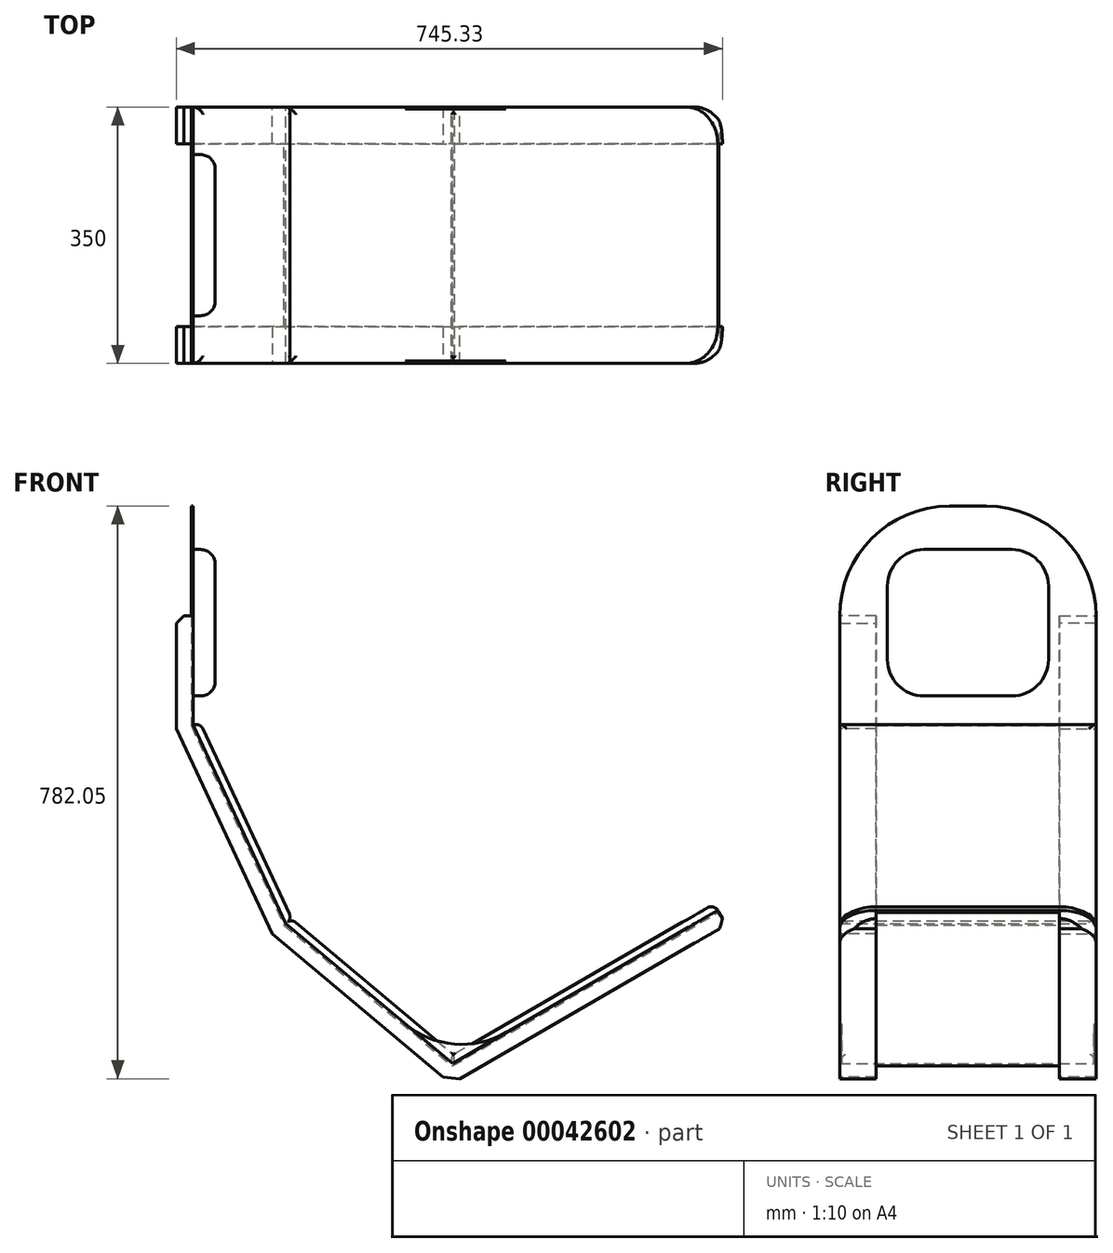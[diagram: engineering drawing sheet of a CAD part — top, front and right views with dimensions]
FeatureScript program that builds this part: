
annotation { "Feature Type Name" : "Feature", "Feature Type Description" : "" }
export const myFeature = defineFeature(function(context is Context, id is Id, definition is map)
    precondition{}
    {
        {
            var Q0;
            Q0=qCreatedBy(makeId("Front.planeOp"),FACE);
            var sketch = newSketch(context, id + "F0", { "sketchPlane" : qUnion([Q0])});
            skLineSegment(sketch, "E0", {"start": v(0, 770) * mm, "end": v(0, 0) * mm, "construction": true});
            skLineSegment(sketch, "E1", {"start": v(0, 770) * mm, "end": v(0, 470) * mm});
            skLineSegment(sketch, "E2", {"start": v(0, 470) * mm, "end": v(126.79, 198.1) * mm});
            skLineSegment(sketch, "E3", {"start": v(126.79, 198.1) * mm, "end": v(356.6, 5.27) * mm});
            skLineSegment(sketch, "E4", {"start": v(356.6, 5.27) * mm, "end": v(720.33, 215.27) * mm});
            skLineSegment(sketch, "E5", {"start": v(0, 0) * mm, "end": v(1241.59, 0) * mm, "construction": true});
            skLineSegment(sketch, "E6.0", {"start": v(356.92, 8.92) * mm, "end": v(718.83, 217.87) * mm});
            skLineSegment(sketch, "E6.1", {"start": v(129.22, 199.98) * mm, "end": v(356.92, 8.92) * mm});
            skLineSegment(sketch, "E6.2", {"start": v(3, 470.67) * mm, "end": v(129.22, 199.98) * mm});
            skLineSegment(sketch, "E6.3", {"start": v(3, 770) * mm, "end": v(3, 470.67) * mm});
            skLineSegment(sketch, "E7", {"start": v(718.83, 217.87) * mm, "end": v(720.33, 215.27) * mm});
            skLineSegment(sketch, "E8", {"start": v(0, 770) * mm, "end": v(3, 770) * mm});
            skSolve(sketch);
        }
        {
            var Q0;
            Q0=qSketchRegion(id+"F0",true);
            extrude(context, id + "F1", {"entities" : qUnion([Q0]), "endBound" : BoundingType.SYMMETRIC, "depth" : 350 * mm});
        }
        {
            var Q0;
            Q0=makeQuery(id+"F1.opExtrude","CAP_EDGE",EDGE,{"disambiguationData":[OSD([sQuery(id+"F0.wireOp",EDGE,"E8")])],"isStart":false});
            var Q1;
            Q1=makeQuery(id+"F1.opExtrude","CAP_EDGE",EDGE,{"disambiguationData":[OSD([sQuery(id+"F0.wireOp",EDGE,"E8")])],"isStart":true});
            fillet(context, id + "F2", {"entities" : qUnion([Q0, Q1]), "radius" : 150 * mm, "tangentPropagation" : true, "allowEdgeOverflow" : false});
        }
        {
            var Q0;
            Q0=makeQuery(id+"F1.opExtrude","CAP_FACE",FACE,{"disambiguationData":[OSD([sQuery(id+"F0.wireOp",EDGE,"E1"),sQuery(id+"F0.wireOp",EDGE,"E2"),sQuery(id+"F0.wireOp",EDGE,"E3"),sQuery(id+"F0.wireOp",EDGE,"E4"),sQuery(id+"F0.wireOp",EDGE,"E6.0"),sQuery(id+"F0.wireOp",EDGE,"E6.1"),sQuery(id+"F0.wireOp",EDGE,"E6.2"),sQuery(id+"F0.wireOp",EDGE,"E6.3"),sQuery(id+"F0.wireOp",EDGE,"E7"),sQuery(id+"F0.wireOp",EDGE,"E8")])],"isStart":false});
            var sketch = newSketch(context, id + "F3", { "sketchPlane" : qUnion([Q0])});
            skLineSegment(sketch, "E9.0", {"start": v(129.22, 199.98) * mm, "end": v(356.92, 8.92) * mm});
            skLineSegment(sketch, "E9.1", {"start": v(356.92, 8.92) * mm, "end": v(718.83, 217.87) * mm});
            skArc(sketch, "E10", {"start": v(292.55, 62.93) * mm, "mid": v(359.23, 35.31) * mm, "end": v(429.69, 50.93) * mm});
            skSolve(sketch);
        }
        {
            var Q0;
            Q0=qSketchRegion(id+"F3",true);
            extrude(context, id + "F4", {"entities" : qUnion([Q0]), "oppositeDirection" : true, "depth" : 3 * mm});
        }
        {
            var Q0;
            Q0=makeQuery(id+"F4.opExtrude","SWEPT_BODY",BODY,{"disambiguationData":[OSD([sQuery(id+"F3.wireOp",EDGE,"E9.0"),sQuery(id+"F3.wireOp",EDGE,"E9.1"),sQuery(id+"F3.wireOp",EDGE,"E10")])]});
            var Q1;
            Q1=qCreatedBy(makeId("Front.planeOp"),FACE);
            mirror(context, id + "F5", {"entities" : qUnion([Q0]), "mirrorPlane" : qUnion([Q1])});
        }
        {
            var Q0;
            Q0=makeQuery(id+"F1.opExtrude","CAP_FACE",FACE,{"disambiguationData":[OSD([sQuery(id+"F0.wireOp",EDGE,"E1"),sQuery(id+"F0.wireOp",EDGE,"E2"),sQuery(id+"F0.wireOp",EDGE,"E3"),sQuery(id+"F0.wireOp",EDGE,"E4"),sQuery(id+"F0.wireOp",EDGE,"E6.0"),sQuery(id+"F0.wireOp",EDGE,"E6.1"),sQuery(id+"F0.wireOp",EDGE,"E6.2"),sQuery(id+"F0.wireOp",EDGE,"E6.3"),sQuery(id+"F0.wireOp",EDGE,"E7"),sQuery(id+"F0.wireOp",EDGE,"E8")])],"isStart":false});
            var sketch = newSketch(context, id + "F6", { "sketchPlane" : qUnion([Q0])});
            skLineSegment(sketch, "E11.0.2", {"start": v(0, 620) * mm, "end": v(0, 470) * mm});
            skLineSegment(sketch, "E11.0.4", {"start": v(0, 470) * mm, "end": v(0, 620) * mm});
            skLineSegment(sketch, "E11.1.0", {"start": v(0, 470) * mm, "end": v(126.79, 198.1) * mm});
            skLineSegment(sketch, "E11.1.2", {"start": v(126.79, 198.1) * mm, "end": v(0, 470) * mm});
            skLineSegment(sketch, "E11.2.0", {"start": v(126.79, 198.1) * mm, "end": v(356.6, 5.27) * mm});
            skLineSegment(sketch, "E11.2.2", {"start": v(356.6, 5.27) * mm, "end": v(126.79, 198.1) * mm});
            skLineSegment(sketch, "E11.3.0", {"start": v(356.6, 5.27) * mm, "end": v(720.33, 215.27) * mm});
            skLineSegment(sketch, "E11.3.2", {"start": v(720.33, 215.27) * mm, "end": v(356.6, 5.27) * mm});
            skLineSegment(sketch, "E12.0", {"start": v(-20, 465.57) * mm, "end": v(-20, 620) * mm});
            skLineSegment(sketch, "E12.1", {"start": v(110.53, 185.64) * mm, "end": v(-20, 465.57) * mm});
            skLineSegment(sketch, "E12.2", {"start": v(354.47, -19.05) * mm, "end": v(110.53, 185.64) * mm});
            skLineSegment(sketch, "E12.3", {"start": v(730.33, 197.95) * mm, "end": v(354.47, -19.05) * mm});
            skLineSegment(sketch, "E13", {"start": v(0, 620) * mm, "end": v(-20, 620) * mm});
            skLineSegment(sketch, "E14", {"start": v(720.33, 215.27) * mm, "end": v(730.33, 197.95) * mm});
            skSolve(sketch);
        }
        {
            var Q0;
            Q0=qSketchRegion(id+"F6",true);
            extrude(context, id + "F7", {"entities" : qUnion([Q0]), "oppositeDirection" : true, "depth" : 50 * mm});
        }
        {
            var Q0;
            Q0=makeQuery(id+"F7.opExtrude","SWEPT_EDGE",EDGE,{"disambiguationData":[OSD([sQuery(id+"F6.wireOp",EDGE,"E12.0"),sQuery(id+"F6.wireOp",EDGE,"E13")])]});
            var Q1;
            Q1=makeQuery(id+"F7.opExtrude","SWEPT_EDGE",EDGE,{"disambiguationData":[OSD([sQuery(id+"F6.wireOp",EDGE,"E12.3"),sQuery(id+"F6.wireOp",EDGE,"E14")])]});
            chamfer(context, id + "F8", {"entities" : qUnion([Q0, Q1]), "width" : 10 * mm, "tangentPropagation" : true});
        }
        {
            var Q0;
            Q0=makeQuery(id+"F7.opExtrude","SWEPT_BODY",BODY,{"disambiguationData":[OSD([sQuery(id+"F6.wireOp",EDGE,"E11.0.4"),sQuery(id+"F6.wireOp",EDGE,"E11.1.2"),sQuery(id+"F6.wireOp",EDGE,"E11.2.2"),sQuery(id+"F6.wireOp",EDGE,"E11.3.2"),sQuery(id+"F6.wireOp",EDGE,"E12.0"),sQuery(id+"F6.wireOp",EDGE,"E12.1"),sQuery(id+"F6.wireOp",EDGE,"E12.2"),sQuery(id+"F6.wireOp",EDGE,"E12.3"),sQuery(id+"F6.wireOp",EDGE,"E13"),sQuery(id+"F6.wireOp",EDGE,"E14")])]});
            var Q1;
            Q1=qCreatedBy(makeId("Front.planeOp"),FACE);
            mirror(context, id + "F9", {"operationType" : NewBodyOperationType.ADD, "entities" : qUnion([Q0]), "mirrorPlane" : qUnion([Q1])});
        }
        {
            var Q0;
            Q0=makeQuery(id+"F1.opExtrude","CAP_EDGE",EDGE,{"disambiguationData":[OSD([sQuery(id+"F0.wireOp",EDGE,"E7")])],"isStart":false});
            var Q1;
            Q1=makeQuery(id+"F1.opExtrude","CAP_EDGE",EDGE,{"disambiguationData":[OSD([sQuery(id+"F0.wireOp",EDGE,"E7")])],"isStart":true});
            fillet(context, id + "F10", {"entities" : qUnion([Q0, Q1]), "radius" : 50 * mm, "tangentPropagation" : true, "allowEdgeOverflow" : false});
        }
        {
            var Q0;
            Q0=makeQuery(id+"F1.opExtrude","SWEPT_FACE",FACE,{"disambiguationData":[OSD([sQuery(id+"F0.wireOp",EDGE,"E6.3")])]});
            var sketch = newSketch(context, id + "F11", { "sketchPlane" : qUnion([Q0])});
            skLineSegment(sketch, "E15.rect.bottom", {"start": v(60, 510.67) * mm, "end": v(-60, 510.67) * mm});
            skLineSegment(sketch, "E15.rect.top", {"start": v(60, 710.67) * mm, "end": v(-60, 710.67) * mm});
            skLineSegment(sketch, "E15.rect.left", {"start": v(110, 560.67) * mm, "end": v(110, 660.67) * mm});
            skLineSegment(sketch, "E15.rect.right", {"start": v(-110, 560.67) * mm, "end": v(-110, 660.67) * mm});
            skPoint(sketch, "E15.rect.middle", {"position": v(0, 610.67) * mm});
            skPoint(sketch, "E16.visualSharp", {"position": v(-110, 710.67) * mm});
            skArc(sketch, "E16.filletArc", {"start": v(-60, 710.67) * mm, "mid": v(-95.36, 696.02) * mm, "end": v(-110, 660.67) * mm});
            skPoint(sketch, "E17.visualSharp", {"position": v(110, 710.67) * mm});
            skArc(sketch, "E17.filletArc", {"start": v(110, 660.67) * mm, "mid": v(95.36, 696.02) * mm, "end": v(60, 710.67) * mm});
            skPoint(sketch, "E18.visualSharp", {"position": v(-110, 510.67) * mm});
            skArc(sketch, "E18.filletArc", {"start": v(-110, 560.67) * mm, "mid": v(-95.36, 525.3) * mm, "end": v(-60, 510.67) * mm});
            skPoint(sketch, "E19.visualSharp", {"position": v(110, 510.67) * mm});
            skArc(sketch, "E19.filletArc", {"start": v(60, 510.67) * mm, "mid": v(95.36, 525.3) * mm, "end": v(110, 560.67) * mm});
            skSolve(sketch);
        }
        {
            var Q0;
            Q0=qSketchRegion(id+"F11",true);
            extrude(context, id + "F12", {"entities" : qUnion([Q0]), "depth" : 30 * mm});
        }
        {
            var Q0;
            Q0=makeQuery(id+"F12.opExtrude","CAP_FACE",FACE,{"disambiguationData":[OSD([sQuery(id+"F11.wireOp",EDGE,"E15.rect.bottom"),sQuery(id+"F11.wireOp",EDGE,"E15.rect.top"),sQuery(id+"F11.wireOp",EDGE,"E15.rect.left"),sQuery(id+"F11.wireOp",EDGE,"E15.rect.right"),sQuery(id+"F11.wireOp",EDGE,"E16.filletArc"),sQuery(id+"F11.wireOp",EDGE,"E17.filletArc"),sQuery(id+"F11.wireOp",EDGE,"E18.filletArc"),sQuery(id+"F11.wireOp",EDGE,"E19.filletArc")])],"isStart":false});
            fillet(context, id + "F13", {"entities" : qUnion([Q0]), "radius" : 20 * mm, "tangentPropagation" : true, "allowEdgeOverflow" : false});
        }
        {
            var Q0;
            Q0=makeQuery(id+"F1.opExtrude","SWEPT_FACE",FACE,{"disambiguationData":[OSD([sQuery(id+"F0.wireOp",EDGE,"E6.2")])]});
            var sketch = newSketch(context, id + "F14", { "sketchPlane" : qUnion([Q0])});
            skLineSegment(sketch, "E20.rect.bottom", {"start": v(175, 126.63) * mm, "end": v(-175, 126.63) * mm});
            skLineSegment(sketch, "E20.rect.top", {"start": v(175, 425.3) * mm, "end": v(-175, 425.3) * mm});
            skLineSegment(sketch, "E20.rect.left", {"start": v(175, 126.63) * mm, "end": v(175, 425.3) * mm});
            skLineSegment(sketch, "E20.rect.right", {"start": v(-175, 126.63) * mm, "end": v(-175, 425.3) * mm});
            skPoint(sketch, "E20.rect.middle", {"position": v(0, 275.96) * mm});
            skSolve(sketch);
        }
        {
            var Q0;
            Q0=qSketchRegion(id+"F14",true);
            extrude(context, id + "F15", {"entities" : qUnion([Q0]), "depth" : 10 * mm});
        }
        {
            var Q0;
            Q0=makeQuery(id+"F15.opExtrude","CAP_FACE",FACE,{"disambiguationData":[OSD([sQuery(id+"F14.wireOp",EDGE,"E20.rect.bottom"),sQuery(id+"F14.wireOp",EDGE,"E20.rect.top"),sQuery(id+"F14.wireOp",EDGE,"E20.rect.left"),sQuery(id+"F14.wireOp",EDGE,"E20.rect.right")])],"isStart":false});
            fillet(context, id + "F16", {"entities" : qUnion([Q0]), "radius" : 10 * mm, "tangentPropagation" : true, "allowEdgeOverflow" : false});
        }
        {
            var Q0;
            Q0=makeQuery(id+"F1.opExtrude","SWEPT_FACE",FACE,{"disambiguationData":[OSD([sQuery(id+"F0.wireOp",EDGE,"E6.1")])]});
            extrude(context, id + "F17", {"entities" : qUnion([Q0]), "depth" : 10 * mm});
        }
        {
            var Q0;
            Q0=makeQuery(id+"F17.opExtrude","CAP_FACE",FACE,{"disambiguationData":[OSD([sQuery(id+"F0.wireOp",EDGE,"E6.1")])],"isStart":false});
            fillet(context, id + "F18", {"entities" : qUnion([Q0]), "radius" : 10 * mm, "tangentPropagation" : true, "allowEdgeOverflow" : false});
        }
        {
            var Q0;
            Q0=makeQuery(id+"F1.opExtrude","SWEPT_FACE",FACE,{"disambiguationData":[OSD([sQuery(id+"F0.wireOp",EDGE,"E6.0")])]});
            extrude(context, id + "F19", {"entities" : qUnion([Q0]), "depth" : 10 * mm});
        }
        {
            var Q0;
            Q0=makeQuery(id+"F19.opExtrude","CAP_FACE",FACE,{"disambiguationData":[OSD([sQuery(id+"F0.wireOp",EDGE,"E6.0")])],"isStart":false});
            fillet(context, id + "F20", {"entities" : qUnion([Q0]), "radius" : 10 * mm, "tangentPropagation" : true, "allowEdgeOverflow" : false});
        }
        {
            var Q0;
            Q0=makeQuery(id+"F7.opExtrude","SWEPT_EDGE",EDGE,{"disambiguationData":[OSD([sQuery(id+"F6.wireOp",EDGE,"E12.2"),sQuery(id+"F6.wireOp",EDGE,"E12.3")])]});
            var Q1;
            Q1=makeQuery(id+"F9.opPattern","COPY",EDGE,{"derivedFrom":makeQuery(id+"F7.opExtrude","SWEPT_EDGE",EDGE,{"disambiguationData":[OSD([sQuery(id+"F6.wireOp",EDGE,"E12.2"),sQuery(id+"F6.wireOp",EDGE,"E12.3")])]}),"instanceName":"1"});
            chamfer(context, id + "F21", {"entities" : qUnion([Q0, Q1]), "width" : 20 * mm, "tangentPropagation" : true});
        }
    });
